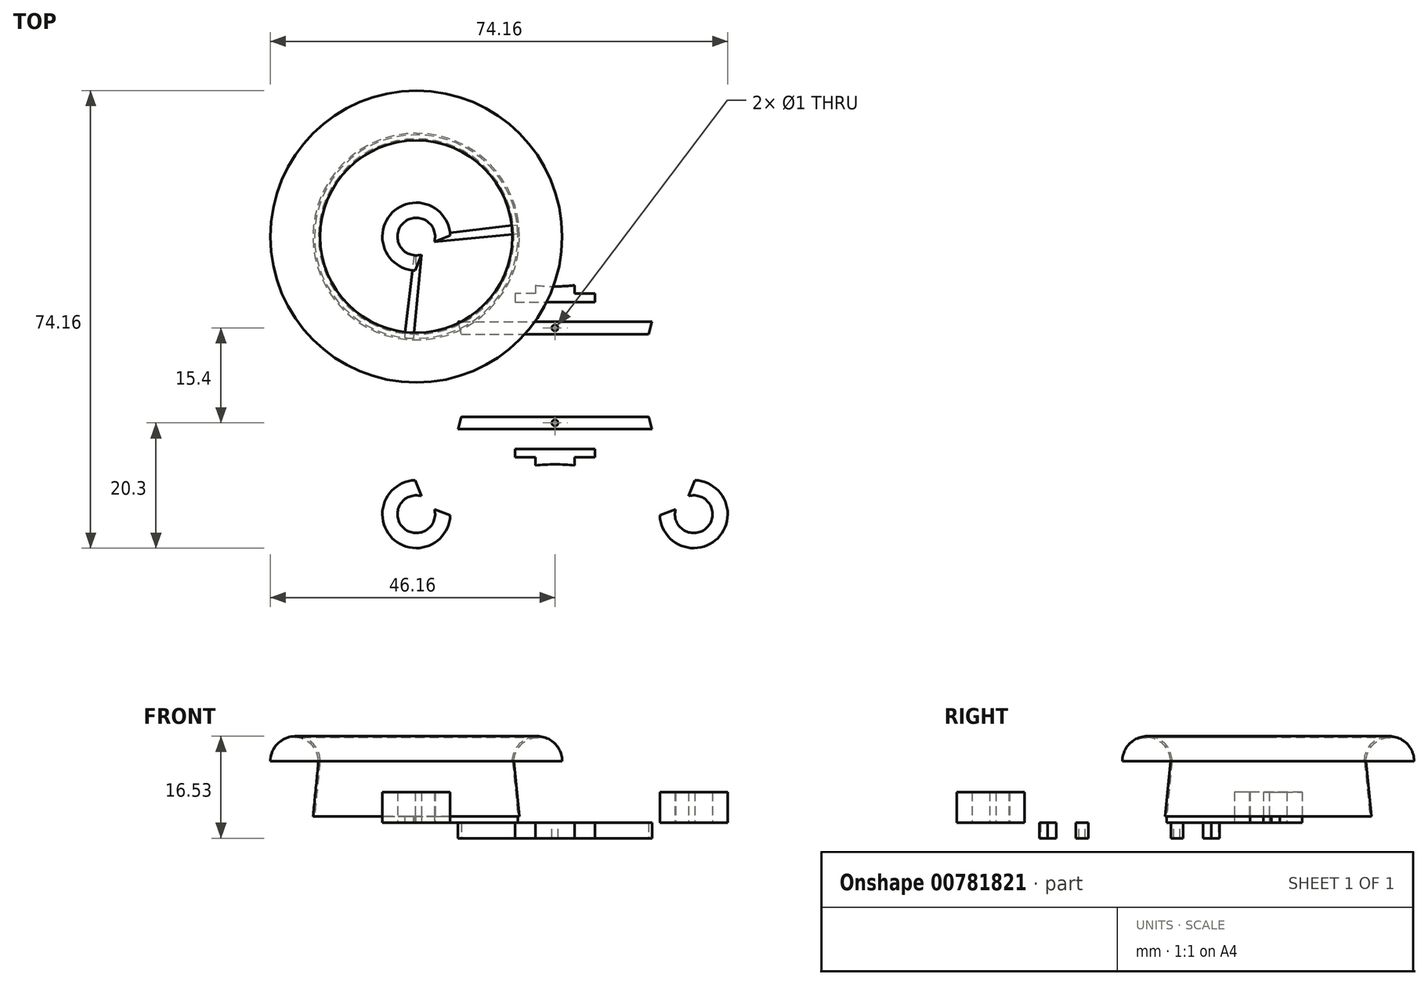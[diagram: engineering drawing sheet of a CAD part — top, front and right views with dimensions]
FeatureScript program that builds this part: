
annotation { "Feature Type Name" : "Feature", "Feature Type Description" : "" }
export const myFeature = defineFeature(function(context is Context, id is Id, definition is map)
    precondition{}
    {
        {
            var Q0;
            Q0=qCreatedBy(makeId("Top.planeOp"),FACE);
            var sketch = newSketch(context, id + "F0", { "sketchPlane" : qUnion([Q0])});
            skCircle(sketch, "E0", {"center": v(-22.5, 22.5) * mm, "radius": 3.05 * mm});
            skCircle(sketch, "E1", {"center": v(22.5, 22.5) * mm, "radius": 3.05 * mm});
            skCircle(sketch, "E2", {"center": v(-22.5, -22.5) * mm, "radius": 3.05 * mm});
            skCircle(sketch, "E3", {"center": v(22.5, -22.5) * mm, "radius": 3.05 * mm});
            skLineSegment(sketch, "E4", {"start": v(-22.5, 22.5) * mm, "end": v(22.5, -22.5) * mm, "construction": true});
            skLineSegment(sketch, "E5", {"start": v(-22.5, -22.5) * mm, "end": v(22.5, 22.5) * mm, "construction": true});
            skPoint(sketch, "E6", {"position": v(0, 0) * mm});
            skArc(sketch, "E7", {"start": v(-21.68, -19.56) * mm, "mid": v(-14.43, 0) * mm, "end": v(-21.68, 19.56) * mm});
            skArc(sketch, "E8", {"start": v(-19.56, 21.68) * mm, "mid": v(0, 14.43) * mm, "end": v(19.56, 21.68) * mm});
            skArc(sketch, "E9", {"start": v(21.68, 19.56) * mm, "mid": v(14.43, 0) * mm, "end": v(21.68, -19.56) * mm});
            skArc(sketch, "E10", {"start": v(19.56, -21.68) * mm, "mid": v(0, -14.43) * mm, "end": v(-19.56, -21.68) * mm});
            skLineSegment(sketch, "E11", {"start": v(-19.56, 21.68) * mm, "end": v(-21.68, 19.56) * mm, "construction": true});
            skLineSegment(sketch, "E12", {"start": v(19.56, 21.68) * mm, "end": v(21.68, 19.56) * mm, "construction": true});
            skLineSegment(sketch, "E13", {"start": v(21.68, -19.56) * mm, "end": v(19.56, -21.68) * mm, "construction": true});
            skLineSegment(sketch, "E14", {"start": v(-19.56, -21.68) * mm, "end": v(-21.68, -19.56) * mm, "construction": true});
            skArc(sketch, "E15", {"start": v(-22.66, 17) * mm, "mid": v(-26.39, 26.39) * mm, "end": v(-17, 22.66) * mm});
            skArc(sketch, "E16", {"start": v(17, 22.66) * mm, "mid": v(26.39, 26.39) * mm, "end": v(22.66, 17) * mm});
            skArc(sketch, "E17", {"start": v(22.66, -17) * mm, "mid": v(26.39, -26.39) * mm, "end": v(17, -22.66) * mm});
            skArc(sketch, "E18", {"start": v(-17, -22.66) * mm, "mid": v(-26.39, -26.39) * mm, "end": v(-22.66, -17) * mm});
            skArc(sketch, "E19", {"start": v(-22.66, -17) * mm, "mid": v(-17.38, 0) * mm, "end": v(-22.66, 17) * mm});
            skArc(sketch, "E20", {"start": v(-17, 22.66) * mm, "mid": v(0, 17.38) * mm, "end": v(17, 22.66) * mm});
            skArc(sketch, "E21", {"start": v(22.66, 17) * mm, "mid": v(17.38, 0) * mm, "end": v(22.66, -17) * mm});
            skArc(sketch, "E22", {"start": v(17, -22.66) * mm, "mid": v(0, -17.38) * mm, "end": v(-17, -22.66) * mm});
            skLineSegment(sketch, "E23", {"start": v(-17, 22.66) * mm, "end": v(-22.66, 17) * mm, "construction": true});
            skLineSegment(sketch, "E24", {"start": v(17, 22.66) * mm, "end": v(22.66, 17) * mm, "construction": true});
            skLineSegment(sketch, "E25", {"start": v(22.66, -17) * mm, "end": v(17, -22.66) * mm, "construction": true});
            skLineSegment(sketch, "E26", {"start": v(-17, -22.66) * mm, "end": v(-22.66, -17) * mm, "construction": true});
            skLineSegment(sketch, "E27", {"start": v(-15.19, 6.7) * mm, "end": v(15.19, 6.7) * mm});
            skLineSegment(sketch, "E28", {"start": v(-15.72, -8.7) * mm, "end": v(15.72, -8.7) * mm});
            skLineSegment(sketch, "E29", {"start": v(-15.19, -6.7) * mm, "end": v(15.19, -6.7) * mm});
            skLineSegment(sketch, "E30", {"start": v(-15.72, 8.7) * mm, "end": v(15.72, 8.7) * mm});
            skLineSegment(sketch, "E31", {"start": v(0, 8.7) * mm, "end": v(0, 6.7) * mm, "construction": true});
            skLineSegment(sketch, "E32", {"start": v(0, -6.7) * mm, "end": v(0, -8.7) * mm, "construction": true});
            skLineSegment(sketch, "E33", {"start": v(0, 6.7) * mm, "end": v(0, 0) * mm, "construction": true});
            skLineSegment(sketch, "E34", {"start": v(0, 0) * mm, "end": v(0, -6.7) * mm, "construction": true});
            skSolve(sketch);
        }
        {
            var Q0;
            Q0=makeQuery(id+"F0.imprint","IMPRINT",FACE,{"disambiguationData":[TD([[makeQuery(id+"F0.imprint","IMPRINT",EDGE,{"derivedFrom":sQuery(id+"F0.wireOp",EDGE,"Eu03rFA7-vXEY-t7IH-vWco-ZoA1tHDgax1W")}),-1.0]])]});
            var Q1;
            {var subQ3=sQuery(id+"F0.wireOp",EDGE,"E7");Q1=makeQuery(id+"F0.imprint","IMPRINT",FACE,{"disambiguationData":[TD([[makeQuery(id+"F0.imprint","IMPRINT",EDGE,{"derivedFrom":subQ3}),1.0]])]});}
            var Q2;
            {var subQ0=sQuery(id+"F0.wireOp",EDGE,"E27");Q2=makeQuery(id+"F0.imprint","IMPRINT",FACE,{"disambiguationData":[TD([[makeQuery(id+"F0.imprint","IMPRINT",EDGE,{"derivedFrom":subQ0}),1.0]])]});}
            var Q3;
            {var subQ0=sQuery(id+"F0.wireOp",EDGE,"E28");Q3=makeQuery(id+"F0.imprint","IMPRINT",FACE,{"disambiguationData":[TD([[makeQuery(id+"F0.imprint","IMPRINT",EDGE,{"derivedFrom":subQ0}),1.0]])]});}
            extrude(context, id + "F1", {"entities" : qUnion([Q0, Q1, Q2, Q3]), "depth" : 2.5 * mm, "offsetDistance" : 25 * mm});
        }
        {
            var Q0;
            Q0=makeQuery(id+"F1.opExtrude","CAP_FACE",FACE,{"disambiguationData":[OSD([sQuery(id+"F0.wireOp",EDGE,"E0"),sQuery(id+"F0.wireOp",EDGE,"E1"),sQuery(id+"F0.wireOp",EDGE,"E2"),sQuery(id+"F0.wireOp",EDGE,"E3"),sQuery(id+"F0.wireOp",EDGE,"E7"),sQuery(id+"F0.wireOp",EDGE,"E8"),sQuery(id+"F0.wireOp",EDGE,"E9"),sQuery(id+"F0.wireOp",EDGE,"E10"),sQuery(id+"F0.wireOp",EDGE,"E15"),sQuery(id+"F0.wireOp",EDGE,"E16"),sQuery(id+"F0.wireOp",EDGE,"E17"),sQuery(id+"F0.wireOp",EDGE,"E18"),sQuery(id+"F0.wireOp",EDGE,"E19"),sQuery(id+"F0.wireOp",EDGE,"E20"),sQuery(id+"F0.wireOp",EDGE,"E21"),sQuery(id+"F0.wireOp",EDGE,"E22")])],"isStart":false});
            var sketch = newSketch(context, id + "F2", { "sketchPlane" : qUnion([Q0])});
            skArc(sketch, "E35.0", {"start": v(-19.56, 21.68) * mm, "mid": v(-24.66, 24.66) * mm, "end": v(-21.68, 19.56) * mm});
            skArc(sketch, "E36.0", {"start": v(-22.66, 17) * mm, "mid": v(-26.39, 26.39) * mm, "end": v(-17, 22.66) * mm});
            skArc(sketch, "E37.0", {"start": v(17, 22.66) * mm, "mid": v(26.39, 26.39) * mm, "end": v(22.66, 17) * mm});
            skArc(sketch, "E38.0", {"start": v(21.68, 19.56) * mm, "mid": v(24.66, 24.66) * mm, "end": v(19.56, 21.68) * mm});
            skArc(sketch, "E39.0", {"start": v(19.56, -21.68) * mm, "mid": v(24.66, -24.66) * mm, "end": v(21.68, -19.56) * mm});
            skArc(sketch, "E40.0", {"start": v(-21.68, -19.56) * mm, "mid": v(-24.66, -24.66) * mm, "end": v(-19.56, -21.68) * mm});
            skArc(sketch, "E41.0", {"start": v(-17, -22.66) * mm, "mid": v(-26.39, -26.39) * mm, "end": v(-22.66, -17) * mm});
            skLineSegment(sketch, "E42", {"start": v(-22.66, -17) * mm, "end": v(-21.68, -19.56) * mm});
            skLineSegment(sketch, "E43", {"start": v(-19.56, -21.68) * mm, "end": v(-17, -22.66) * mm});
            skLineSegment(sketch, "E44", {"start": v(19.56, -21.68) * mm, "end": v(17, -22.66) * mm});
            skArc(sketch, "E45.0", {"start": v(22.66, -17) * mm, "mid": v(26.39, -26.39) * mm, "end": v(17, -22.66) * mm});
            skLineSegment(sketch, "E46", {"start": v(21.68, -19.56) * mm, "end": v(22.66, -17) * mm});
            skLineSegment(sketch, "E47", {"start": v(19.56, 21.68) * mm, "end": v(17, 22.66) * mm});
            skLineSegment(sketch, "E48", {"start": v(21.68, 19.56) * mm, "end": v(22.66, 17) * mm});
            skLineSegment(sketch, "E49", {"start": v(-19.56, 21.68) * mm, "end": v(-17, 22.66) * mm});
            skLineSegment(sketch, "E50", {"start": v(-21.68, 19.56) * mm, "end": v(-22.66, 17) * mm});
            skSolve(sketch);
        }
        {
            var Q0;
            Q0=makeQuery(id+"F2.imprint","IMPRINT",FACE,{"disambiguationData":[TD([[makeQuery(id+"F2.imprint","IMPRINT",EDGE,{"derivedFrom":sQuery(id+"F2.wireOp",EDGE,"E35.0")}),-1.0]])]});
            var Q1;
            Q1=makeQuery(id+"F2.imprint","IMPRINT",FACE,{"disambiguationData":[TD([[makeQuery(id+"F2.imprint","IMPRINT",EDGE,{"derivedFrom":sQuery(id+"F2.wireOp",EDGE,"E40.0")}),-1.0]])]});
            var Q2;
            Q2=makeQuery(id+"F2.imprint","IMPRINT",FACE,{"disambiguationData":[TD([[makeQuery(id+"F2.imprint","IMPRINT",EDGE,{"derivedFrom":sQuery(id+"F2.wireOp",EDGE,"E39.0")}),-1.0]])]});
            var Q3;
            Q3=makeQuery(id+"F2.imprint","IMPRINT",FACE,{"disambiguationData":[TD([[makeQuery(id+"F2.imprint","IMPRINT",EDGE,{"derivedFrom":sQuery(id+"F2.wireOp",EDGE,"E37.0")}),-1.0]])]});
            extrude(context, id + "F3", {"entities" : qUnion([Q0, Q1, Q2, Q3]), "operationType" : NewBodyOperationType.ADD, "depth" : 5 * mm, "offsetDistance" : 25 * mm});
        }
        {
            var Q0;
            {var subQ0=sQuery(id+"F0.wireOp",EDGE,"E20");var subQ1=sQuery(id+"F0.wireOp",EDGE,"E16");var subQ2=sQuery(id+"F0.wireOp",EDGE,"E0");var subQ3=sQuery(id+"F0.wireOp",EDGE,"E8");var subQ4=sQuery(id+"F0.wireOp",EDGE,"E1");var subQ5=sQuery(id+"F0.wireOp",EDGE,"E15");Q0=makeQuery(id+"F3.boolean.opBoolean","SPLIT",FACE,{"disambiguationData":[TD([makeQuery(id+"F1.opExtrude","SWEPT_FACE",FACE,{"disambiguationData":[OSD([subQ3])]})])],"derivedFrom":makeQuery(id+"F1.opExtrude","CAP_FACE",FACE,{"disambiguationData":[OSD([subQ2,subQ4,sQuery(id+"F0.wireOp",EDGE,"E2"),sQuery(id+"F0.wireOp",EDGE,"E3"),sQuery(id+"F0.wireOp",EDGE,"E7"),subQ3,sQuery(id+"F0.wireOp",EDGE,"E9"),sQuery(id+"F0.wireOp",EDGE,"E10"),subQ5,subQ1,sQuery(id+"F0.wireOp",EDGE,"E17"),sQuery(id+"F0.wireOp",EDGE,"E18"),sQuery(id+"F0.wireOp",EDGE,"E19"),subQ0,sQuery(id+"F0.wireOp",EDGE,"E21"),sQuery(id+"F0.wireOp",EDGE,"E22"),sQuery(id+"F0.wireOp",EDGE,"E27"),sQuery(id+"F0.wireOp",EDGE,"E28"),sQuery(id+"F0.wireOp",EDGE,"E29"),sQuery(id+"F0.wireOp",EDGE,"E30"),sQuery(id+"F0.wireOp",EDGE,"072VSIIA-amS3-N3Qy-Xjli-i1a6k8GFf5qD"),sQuery(id+"F0.wireOp",EDGE,"lPqv6BSD-C8e4-qbhh-7SL3-ri7oPHHM2Q3C"),sQuery(id+"F0.wireOp",EDGE,"GbNNHRDb-ISsA-4iVB-EAEx-EyQIxRsDF5b6"),sQuery(id+"F0.wireOp",EDGE,"ilYPEeiZ-QuVn-sicp-pAOQ-38cyuL9utKnt"),sQuery(id+"F0.wireOp",EDGE,"mN4LnpLT-4NuT-A6PV-BQmd-GACzw9HQKLjq"),sQuery(id+"F0.wireOp",EDGE,"mQzBWAmL-a3qw-feIr-Hp9K-SU5xVcQXr3dl"),sQuery(id+"F0.wireOp",EDGE,"O4zD8QYg-mDPH-K9dE-XG8p-ZxYXDiWpvMop")])],"isStart":false})});}
            var sketch = newSketch(context, id + "F4", { "sketchPlane" : qUnion([Q0])});
            skCircle(sketch, "E51", {"center": v(16, 0) * mm, "radius": 0.5 * mm});
            skCircle(sketch, "E52", {"center": v(-16, 0) * mm, "radius": 0.5 * mm});
            skPoint(sketch, "E53", {"position": v(0, 0) * mm});
            skLineSegment(sketch, "E54", {"start": v(-16, 0) * mm, "end": v(16, 0) * mm, "construction": true});
            skCircle(sketch, "E55", {"center": v(0, 7.7) * mm, "radius": 0.5 * mm});
            skCircle(sketch, "E56", {"center": v(0, -7.7) * mm, "radius": 0.5 * mm});
            skLineSegment(sketch, "E57", {"start": v(0, 7.7) * mm, "end": v(0, -7.7) * mm, "construction": true});
            skLineSegment(sketch, "E58.0", {"start": v(-15.72, 8.7) * mm, "end": v(15.72, 8.7) * mm, "construction": true});
            skLineSegment(sketch, "E58.1", {"start": v(-15.19, 6.7) * mm, "end": v(15.19, 6.7) * mm, "construction": true});
            skLineSegment(sketch, "E59", {"start": v(0, 8.7) * mm, "end": v(0, 6.7) * mm, "construction": true});
            skSolve(sketch);
        }
        {
            var Q0;
            Q0=makeQuery(id+"F4.imprint","IMPRINT",FACE,{"disambiguationData":[TD([[makeQuery(id+"F4.imprint","IMPRINT",EDGE,{"derivedFrom":sQuery(id+"F4.wireOp",EDGE,"E51")}),1.0]])]});
            var Q1;
            Q1=makeQuery(id+"F4.imprint","IMPRINT",FACE,{"disambiguationData":[TD([[makeQuery(id+"F4.imprint","IMPRINT",EDGE,{"derivedFrom":sQuery(id+"F4.wireOp",EDGE,"E52")}),1.0]])]});
            var Q2;
            Q2=makeQuery(id+"F4.imprint","IMPRINT",FACE,{"disambiguationData":[TD([[makeQuery(id+"F4.imprint","IMPRINT",EDGE,{"derivedFrom":sQuery(id+"F4.wireOp",EDGE,"E55")}),1.0]])]});
            var Q3;
            Q3=makeQuery(id+"F4.imprint","IMPRINT",FACE,{"disambiguationData":[TD([[makeQuery(id+"F4.imprint","IMPRINT",EDGE,{"derivedFrom":sQuery(id+"F4.wireOp",EDGE,"E56")}),1.0]])]});
            extrude(context, id + "F5", {"entities" : qUnion([Q0, Q1, Q2, Q3]), "operationType" : NewBodyOperationType.REMOVE, "oppositeDirection" : true, "depth" : 25 * mm, "offsetDistance" : 25 * mm});
        }
        {
            var Q0;
            Q0=makeQuery(id+"F1.opExtrude","CAP_FACE",FACE,{"disambiguationData":[OSD([sQuery(id+"F0.wireOp",EDGE,"E0"),sQuery(id+"F0.wireOp",EDGE,"E1"),sQuery(id+"F0.wireOp",EDGE,"E2"),sQuery(id+"F0.wireOp",EDGE,"E3"),sQuery(id+"F0.wireOp",EDGE,"E7"),sQuery(id+"F0.wireOp",EDGE,"E8"),sQuery(id+"F0.wireOp",EDGE,"E9"),sQuery(id+"F0.wireOp",EDGE,"E10"),sQuery(id+"F0.wireOp",EDGE,"E15"),sQuery(id+"F0.wireOp",EDGE,"E16"),sQuery(id+"F0.wireOp",EDGE,"E17"),sQuery(id+"F0.wireOp",EDGE,"E18"),sQuery(id+"F0.wireOp",EDGE,"E19"),sQuery(id+"F0.wireOp",EDGE,"E20"),sQuery(id+"F0.wireOp",EDGE,"E21"),sQuery(id+"F0.wireOp",EDGE,"E22"),sQuery(id+"F0.wireOp",EDGE,"E27"),sQuery(id+"F0.wireOp",EDGE,"E28"),sQuery(id+"F0.wireOp",EDGE,"E29"),sQuery(id+"F0.wireOp",EDGE,"E30")])],"isStart":true});
            var sketch = newSketch(context, id + "F6", { "sketchPlane" : qUnion([Q0])});
            skArc(sketch, "E60.0", {"start": v(19.56, 21.68) * mm, "mid": v(0, 14.43) * mm, "end": v(-19.56, 21.68) * mm});
            skArc(sketch, "E61.0", {"start": v(-19.56, -21.68) * mm, "mid": v(0, -14.43) * mm, "end": v(19.56, -21.68) * mm});
            skLineSegment(sketch, "E62", {"start": v(-14.43, 0) * mm, "end": v(14.43, 0) * mm, "construction": true});
            skLineSegment(sketch, "E63", {"start": v(-3.2, -14.6) * mm, "end": v(-3.2, -13.25) * mm});
            skLineSegment(sketch, "E64", {"start": v(-3.2, -13.25) * mm, "end": v(-6.46, -13.25) * mm});
            skLineSegment(sketch, "E65", {"start": v(-6.46, -13.25) * mm, "end": v(-6.46, -11.9) * mm});
            skLineSegment(sketch, "E66", {"start": v(-6.46, -11.9) * mm, "end": v(6.46, -11.9) * mm});
            skLineSegment(sketch, "E67", {"start": v(6.46, -11.9) * mm, "end": v(6.46, -13.25) * mm});
            skLineSegment(sketch, "E68", {"start": v(6.46, -13.25) * mm, "end": v(3.2, -13.25) * mm});
            skLineSegment(sketch, "E69", {"start": v(3.2, -13.25) * mm, "end": v(3.2, -14.6) * mm});
            skLineSegment(sketch, "E70.MirrorCS", {"start": v(-3.2, 14.6) * mm, "end": v(-3.2, 13.25) * mm});
            skLineSegment(sketch, "E71.MirrorCS", {"start": v(-3.2, 13.25) * mm, "end": v(-6.46, 13.25) * mm});
            skLineSegment(sketch, "E72.MirrorCS", {"start": v(-6.46, 13.25) * mm, "end": v(-6.46, 11.9) * mm});
            skLineSegment(sketch, "E73.MirrorCS", {"start": v(-6.46, 11.9) * mm, "end": v(6.46, 11.9) * mm});
            skLineSegment(sketch, "E74.MirrorCS", {"start": v(6.46, 13.25) * mm, "end": v(3.2, 13.25) * mm});
            skLineSegment(sketch, "E75.MirrorCS", {"start": v(6.46, 11.9) * mm, "end": v(6.46, 13.25) * mm});
            skLineSegment(sketch, "E76.MirrorCS", {"start": v(3.2, 13.25) * mm, "end": v(3.2, 14.6) * mm});
            skSolve(sketch);
        }
        {
            var Q0;
            {var subQ0=sQuery(id+"F6.wireOp",EDGE,"4fdf7f82-c092-4cba-99bc-ed8b0ccf26250.MirrorCS");Q0=makeQuery(id+"F6.imprint","IMPRINT",FACE,{"disambiguationData":[TD([[makeQuery(id+"F6.imprint","IMPRINT",EDGE,{"derivedFrom":subQ0}),1.0]])]});}
            var Q1;
            {var subQ0=sQuery(id+"F6.wireOp",EDGE,"LfqIAdHq-ncsL-fV3U-5Ct1-0tUXCH5J3NB8");Q1=makeQuery(id+"F6.imprint","IMPRINT",FACE,{"disambiguationData":[TD([[makeQuery(id+"F6.imprint","IMPRINT",EDGE,{"derivedFrom":subQ0}),-1.0]])]});}
            var Q2;
            {var subQ0=sQuery(id+"F6.wireOp",EDGE,"0P2vFs8I-HFfS-YY51-0Ri8-ijmF1paSgw7m");Q2=makeQuery(id+"F6.imprint","IMPRINT",FACE,{"disambiguationData":[TD([[makeQuery(id+"F6.imprint","IMPRINT",EDGE,{"derivedFrom":subQ0}),1.0]])]});}
            var Q3;
            {var subQ0=sQuery(id+"F6.wireOp",EDGE,"c46b464a-bcca-47bf-a021-7418af6eee5d0.MirrorCS");Q3=makeQuery(id+"F6.imprint","IMPRINT",FACE,{"disambiguationData":[TD([[makeQuery(id+"F6.imprint","IMPRINT",EDGE,{"derivedFrom":subQ0}),-1.0]])]});}
            var Q4;
            {var subQ0=sQuery(id+"F6.wireOp",EDGE,"E63");Q4=makeQuery(id+"F6.imprint","IMPRINT",FACE,{"disambiguationData":[TD([[makeQuery(id+"F6.imprint","IMPRINT",EDGE,{"derivedFrom":subQ0}),-1.0]])]});}
            var Q5;
            {var subQ0=sQuery(id+"F6.wireOp",EDGE,"E70.MirrorCS");Q5=makeQuery(id+"F6.imprint","IMPRINT",FACE,{"disambiguationData":[TD([[makeQuery(id+"F6.imprint","IMPRINT",EDGE,{"derivedFrom":subQ0}),1.0]])]});}
            var Q6;
            {var subQ0=sQuery(id+"F0.wireOp",EDGE,"E22");var subQ1=sQuery(id+"F0.wireOp",EDGE,"E18");var subQ2=sQuery(id+"F0.wireOp",EDGE,"E2");var subQ3=sQuery(id+"F0.wireOp",EDGE,"E10");var subQ4=sQuery(id+"F0.wireOp",EDGE,"E3");var subQ5=sQuery(id+"F0.wireOp",EDGE,"E17");Q6=makeQuery(id+"F3.boolean.opBoolean","SPLIT",FACE,{"disambiguationData":[TD([makeQuery(id+"F1.opExtrude","SWEPT_FACE",FACE,{"disambiguationData":[OSD([subQ3])]})])],"derivedFrom":makeQuery(id+"F1.opExtrude","CAP_FACE",FACE,{"disambiguationData":[OSD([sQuery(id+"F0.wireOp",EDGE,"E0"),sQuery(id+"F0.wireOp",EDGE,"E1"),subQ2,subQ4,sQuery(id+"F0.wireOp",EDGE,"E7"),sQuery(id+"F0.wireOp",EDGE,"E8"),sQuery(id+"F0.wireOp",EDGE,"E9"),subQ3,sQuery(id+"F0.wireOp",EDGE,"E15"),sQuery(id+"F0.wireOp",EDGE,"E16"),subQ5,subQ1,sQuery(id+"F0.wireOp",EDGE,"E19"),sQuery(id+"F0.wireOp",EDGE,"E20"),sQuery(id+"F0.wireOp",EDGE,"E21"),subQ0,sQuery(id+"F0.wireOp",EDGE,"E27"),sQuery(id+"F0.wireOp",EDGE,"E28"),sQuery(id+"F0.wireOp",EDGE,"E29"),sQuery(id+"F0.wireOp",EDGE,"E30")])],"isStart":false})});}
            extrude(context, id + "F7", {"entities" : qUnion([Q0, Q1, Q2, Q3, Q4, Q5]), "operationType" : NewBodyOperationType.ADD, "endBound" : BoundingType.UP_TO_SURFACE, "oppositeDirection" : true, "depth" : 25 * mm, "endBoundEntityFace" : qUnion([Q6]), "offsetDistance" : 25 * mm});
        }
        {
            var Q0;
            {var subQ0=sQuery(id+"F0.wireOp",EDGE,"E30");var subQ1=sQuery(id+"F0.wireOp",EDGE,"E29");var subQ2=sQuery(id+"F0.wireOp",EDGE,"E27");var subQ3=sQuery(id+"F0.wireOp",EDGE,"E21");var subQ4=sQuery(id+"F0.wireOp",EDGE,"E19");var subQ5=sQuery(id+"F0.wireOp",EDGE,"E18");var subQ6=sQuery(id+"F0.wireOp",EDGE,"E17");var subQ7=sQuery(id+"F0.wireOp",EDGE,"E16");var subQ8=sQuery(id+"F0.wireOp",EDGE,"E15");var subQ9=sQuery(id+"F0.wireOp",EDGE,"E2");var subQ10=sQuery(id+"F0.wireOp",EDGE,"E1");var subQ11=sQuery(id+"F0.wireOp",EDGE,"E3");var subQ12=sQuery(id+"F0.wireOp",EDGE,"E28");var subQ13=sQuery(id+"F0.wireOp",EDGE,"E0");var subQ14=sQuery(id+"F0.wireOp",EDGE,"E9");var subQ15=sQuery(id+"F0.wireOp",EDGE,"E7");Q0=makeQuery(id+"F3.boolean.opBoolean","SPLIT",FACE,{"disambiguationData":[TD([makeQuery(id+"F1.opExtrude","SWEPT_FACE",FACE,{"disambiguationData":[OSD([subQ4])]})])],"derivedFrom":makeQuery(id+"F1.opExtrude","CAP_FACE",FACE,{"disambiguationData":[OSD([subQ13,subQ10,subQ9,subQ11,subQ15,sQuery(id+"F0.wireOp",EDGE,"E8"),subQ14,sQuery(id+"F0.wireOp",EDGE,"E10"),subQ8,subQ7,subQ6,subQ5,subQ4,sQuery(id+"F0.wireOp",EDGE,"E20"),subQ3,sQuery(id+"F0.wireOp",EDGE,"E22"),subQ2,subQ12,subQ1,subQ0])],"isStart":false})});}
            var sketch = newSketch(context, id + "F8", { "sketchPlane" : qUnion([Q0])});
            skArc(sketch, "E77.0", {"start": v(-22.66, 17) * mm, "mid": v(-26.39, 26.39) * mm, "end": v(-17, 22.66) * mm});
            skArc(sketch, "E78.0", {"start": v(17, 22.66) * mm, "mid": v(26.39, 26.39) * mm, "end": v(22.66, 17) * mm});
            skArc(sketch, "E79.0", {"start": v(22.66, -17) * mm, "mid": v(26.39, -26.39) * mm, "end": v(17, -22.66) * mm});
            skArc(sketch, "E80.0", {"start": v(-17, -22.66) * mm, "mid": v(-26.39, -26.39) * mm, "end": v(-22.66, -17) * mm});
            skCircle(sketch, "E81", {"center": v(-22.5, 22.5) * mm, "radius": 16.5 * mm});
            skArc(sketch, "E82.0", {"start": v(-19.56, 21.68) * mm, "mid": v(-24.66, 24.66) * mm, "end": v(-21.68, 19.56) * mm});
            skLineSegment(sketch, "E83", {"start": v(-17, 22.66) * mm, "end": v(-19.56, 21.68) * mm});
            skLineSegment(sketch, "E84", {"start": v(-21.68, 19.56) * mm, "end": v(-22.66, 17) * mm});
            skCircle(sketch, "E85", {"center": v(-22.5, 22.5) * mm, "radius": 16.75 * mm});
            skLineSegment(sketch, "E86", {"start": v(-22.5, 22.5) * mm, "end": v(-24.41, 6.11) * mm});
            skLineSegment(sketch, "E87", {"start": v(-22.5, 22.5) * mm, "end": v(-22.98, 6) * mm});
            skLineSegment(sketch, "E88", {"start": v(-22.5, 22.5) * mm, "end": v(-6, 22.98) * mm});
            skLineSegment(sketch, "E89", {"start": v(-22.5, 22.5) * mm, "end": v(-6.11, 24.41) * mm});
            skArc(sketch, "E90", {"start": v(-22.69, 16) * mm, "mid": v(-27.1, 27.1) * mm, "end": v(-16, 22.69) * mm});
            skLineSegment(sketch, "E91", {"start": v(-21.68, 19.56) * mm, "end": v(-22.98, 6) * mm});
            skLineSegment(sketch, "E92", {"start": v(-19.56, 21.68) * mm, "end": v(-6, 22.98) * mm});
            skLineSegment(sketch, "E93", {"start": v(-22.5, 22.5) * mm, "end": v(-22.5, 39.25) * mm, "construction": true});
            skSolve(sketch);
        }
        {
            var Q0;
            {var subQ4=makeQuery(id+"F1.opExtrude","CAP_EDGE",EDGE,{"disambiguationData":[OSD([sQuery(id+"F0.wireOp",EDGE,"E19")])],"isStart":false});var subQ6=sQuery(id+"F8.wireOp",EDGE,"E85");var subQ8=makeQuery(id+"F8.imprint","INTERSECT",VERTEX,{"derivedFrom":[subQ4,subQ6]});Q0=makeQuery(id+"F8.imprint","IMPRINT",FACE,{"disambiguationData":[TD([[makeQuery(id+"F8.imprint","IMPRINT",EDGE,{"disambiguationData":[TD([[subQ8,-1.0]])],"derivedFrom":subQ4}),1.0]])]});}
            var Q1;
            {var subQ4=makeQuery(id+"F1.opExtrude","CAP_EDGE",EDGE,{"disambiguationData":[OSD([sQuery(id+"F0.wireOp",EDGE,"E19")])],"isStart":false});var subQ6=sQuery(id+"F8.wireOp",EDGE,"E85");var subQ8=makeQuery(id+"F8.imprint","INTERSECT",VERTEX,{"derivedFrom":[subQ4,subQ6]});Q1=makeQuery(id+"F8.imprint","IMPRINT",FACE,{"disambiguationData":[TD([[makeQuery(id+"F8.imprint","IMPRINT",EDGE,{"disambiguationData":[TD([[subQ8,-1.0]])],"derivedFrom":subQ4}),-1.0]])]});}
            var Q2;
            {var subQ0=sQuery(id+"F8.wireOp",EDGE,"E88");var subQ1=sQuery(id+"F8.wireOp",EDGE,"E81");var subQ2=makeQuery(id+"F8.imprint","INTERSECT",VERTEX,{"derivedFrom":[subQ1,subQ0]});Q2=makeQuery(id+"F8.imprint","IMPRINT",FACE,{"disambiguationData":[TD([[makeQuery(id+"F8.imprint","IMPRINT",EDGE,{"disambiguationData":[TD([[subQ2,-1.0]])],"derivedFrom":subQ1}),1.0]])]});}
            var Q3;
            {var subQ0=sQuery(id+"F8.wireOp",EDGE,"E86");var subQ1=sQuery(id+"F8.wireOp",EDGE,"E81");var subQ2=makeQuery(id+"F8.imprint","INTERSECT",VERTEX,{"derivedFrom":[subQ1,subQ0]});Q3=makeQuery(id+"F8.imprint","IMPRINT",FACE,{"disambiguationData":[TD([[makeQuery(id+"F8.imprint","IMPRINT",EDGE,{"disambiguationData":[TD([[subQ2,-1.0]])],"derivedFrom":subQ1}),1.0]])]});}
            var Q4;
            {var subQ0=sQuery(id+"F8.wireOp",EDGE,"E86");var subQ1=sQuery(id+"F8.wireOp",EDGE,"E77.0");var subQ2=makeQuery(id+"F8.imprint","INTERSECT",VERTEX,{"derivedFrom":[subQ1,subQ0]});Q4=makeQuery(id+"F8.imprint","IMPRINT",FACE,{"disambiguationData":[TD([[makeQuery(id+"F8.imprint","IMPRINT",EDGE,{"disambiguationData":[TD([[subQ2,-1.0]])],"derivedFrom":subQ1}),1.0]])]});}
            var Q5;
            {var subQ1=sQuery(id+"F8.wireOp",EDGE,"E77.0");var subQ3=sQuery(id+"F8.wireOp",EDGE,"E86");var subQ4=makeQuery(id+"F8.imprint","INTERSECT",VERTEX,{"derivedFrom":[subQ1,subQ3]});Q5=makeQuery(id+"F8.imprint","IMPRINT",FACE,{"disambiguationData":[TD([[makeQuery(id+"F8.imprint","IMPRINT",EDGE,{"disambiguationData":[TD([[subQ4,-1.0]])],"derivedFrom":subQ3}),1.0]])]});}
            var Q6;
            {var subQ1=sQuery(id+"F8.wireOp",EDGE,"E77.0");var subQ3=sQuery(id+"F8.wireOp",EDGE,"E89");var subQ4=makeQuery(id+"F8.imprint","INTERSECT",VERTEX,{"derivedFrom":[subQ1,subQ3]});Q6=makeQuery(id+"F8.imprint","IMPRINT",FACE,{"disambiguationData":[TD([[makeQuery(id+"F8.imprint","IMPRINT",EDGE,{"disambiguationData":[TD([[subQ4,-1.0]])],"derivedFrom":subQ3}),-1.0]])]});}
            var Q7;
            {var subQ0=sQuery(id+"F8.wireOp",EDGE,"E87");var subQ3=makeQuery(id+"F8.imprint","INTERSECT",VERTEX,{"derivedFrom":[subQ0,sQuery(id+"F8.wireOp",EDGE,"E90")]});Q7=makeQuery(id+"F8.imprint","IMPRINT",FACE,{"disambiguationData":[TD([[makeQuery(id+"F8.imprint","IMPRINT",EDGE,{"disambiguationData":[TD([[subQ3,-1.0]])],"derivedFrom":subQ0}),1.0]])]});}
            var Q8;
            {var subQ0=sQuery(id+"F8.wireOp",EDGE,"E84");Q8=makeQuery(id+"F8.imprint","IMPRINT",FACE,{"disambiguationData":[TD([[makeQuery(id+"F8.imprint","IMPRINT",EDGE,{"derivedFrom":subQ0}),1.0]])]});}
            var Q9;
            {var subQ0=sQuery(id+"F8.wireOp",EDGE,"E83");Q9=makeQuery(id+"F8.imprint","IMPRINT",FACE,{"disambiguationData":[TD([[makeQuery(id+"F8.imprint","IMPRINT",EDGE,{"derivedFrom":subQ0}),1.0]])]});}
            extrude(context, id + "F9", {"entities" : qUnion([Q0, Q1, Q2, Q3, Q4, Q5, Q6, Q7, Q8, Q9]), "depth" : 1 * mm, "offsetDistance" : 25 * mm});
        }
        {
            var Q0;
            Q0=makeQuery(id+"F9.opExtrude","CAP_FACE",FACE,{"disambiguationData":[OSD([sQuery(id+"F8.wireOp",EDGE,"E77.0"),sQuery(id+"F8.wireOp",EDGE,"E81"),sQuery(id+"F8.wireOp",EDGE,"E83"),sQuery(id+"F8.wireOp",EDGE,"E84"),sQuery(id+"F8.wireOp",EDGE,"E85"),sQuery(id+"F8.wireOp",EDGE,"E86"),sQuery(id+"F8.wireOp",EDGE,"E89"),sQuery(id+"F8.wireOp",EDGE,"E90"),sQuery(id+"F8.wireOp",EDGE,"E91"),sQuery(id+"F8.wireOp",EDGE,"E92")])],"isStart":false});
            var sketch = newSketch(context, id + "F10", { "sketchPlane" : qUnion([Q0])});
            skCircle(sketch, "E94", {"center": v(-22.5, 22.5) * mm, "radius": 16.5 * mm});
            skCircle(sketch, "E95.0", {"center": v(-22.5, 22.5) * mm, "radius": 16.75 * mm});
            skSolve(sketch);
        }
        {
            var Q0;
            Q0=sQuery(id+"F8.wireOp",EDGE,"E93");
            cPlane(context, id + "F11", {"entities" : qUnion([Q0]), "cplaneType" : CPlaneType.LINE_ANGLE, "offset" : 25 * mm, "angle" : 90 * degree, "width" : 150 * mm, "height" : 150 * mm});
        }
        {
            var Q0;
            Q0=qCreatedBy(id+"F11.planeOp",FACE);
            var sketch = newSketch(context, id + "F12", { "sketchPlane" : qUnion([Q0])});
            skLineSegment(sketch, "E96.0", {"start": v(6, 3.5) * mm, "end": v(39, 3.5) * mm, "construction": true});
            skLineSegment(sketch, "E97.0", {"start": v(5.75, 3.5) * mm, "end": v(39.25, 3.5) * mm, "construction": true});
            skLineSegment(sketch, "E98", {"start": v(39, 3.5) * mm, "end": v(38.1, 12.5) * mm});
            skLineSegment(sketch, "E99", {"start": v(22.5, 3.5) * mm, "end": v(22.5, 25.45) * mm, "construction": true});
            skLineSegment(sketch, "E100", {"start": v(39.25, 3.5) * mm, "end": v(39, 3.5) * mm});
            skLineSegment(sketch, "E101", {"start": v(39.25, 3.5) * mm, "end": v(38.35, 12.5) * mm});
            skArc(sketch, "E102", {"start": v(46.16, 12.5) * mm, "mid": v(42.13, 16.53) * mm, "end": v(38.1, 12.5) * mm});
            skLineSegment(sketch, "E103", {"start": v(38.1, 12.5) * mm, "end": v(38.1, 9.22) * mm, "construction": true});
            skArc(sketch, "E104", {"start": v(46.16, 12.5) * mm, "mid": v(42.25, 16.32) * mm, "end": v(38.35, 12.5) * mm});
            skSolve(sketch);
        }
        {
            var Q0;
            Q0=makeQuery(id+"F12.imprint","IMPRINT",FACE,{"disambiguationData":[TD([[makeQuery(id+"F12.imprint","IMPRINT",EDGE,{"derivedFrom":sQuery(id+"F12.wireOp",EDGE,"E98")}),-1.0]])]});
            var Q1;
            Q1=sQuery(id+"F12.wireOp",EDGE,"E99");
            revolve(context, id + "F13", {"operationType" : NewBodyOperationType.ADD, "surfaceOperationType" : NewSurfaceOperationType.NEW, "entities" : qUnion([Q0]), "axis" : qUnion([Q1]), "revolveType" : RevolveType.FULL});
        }
    });
